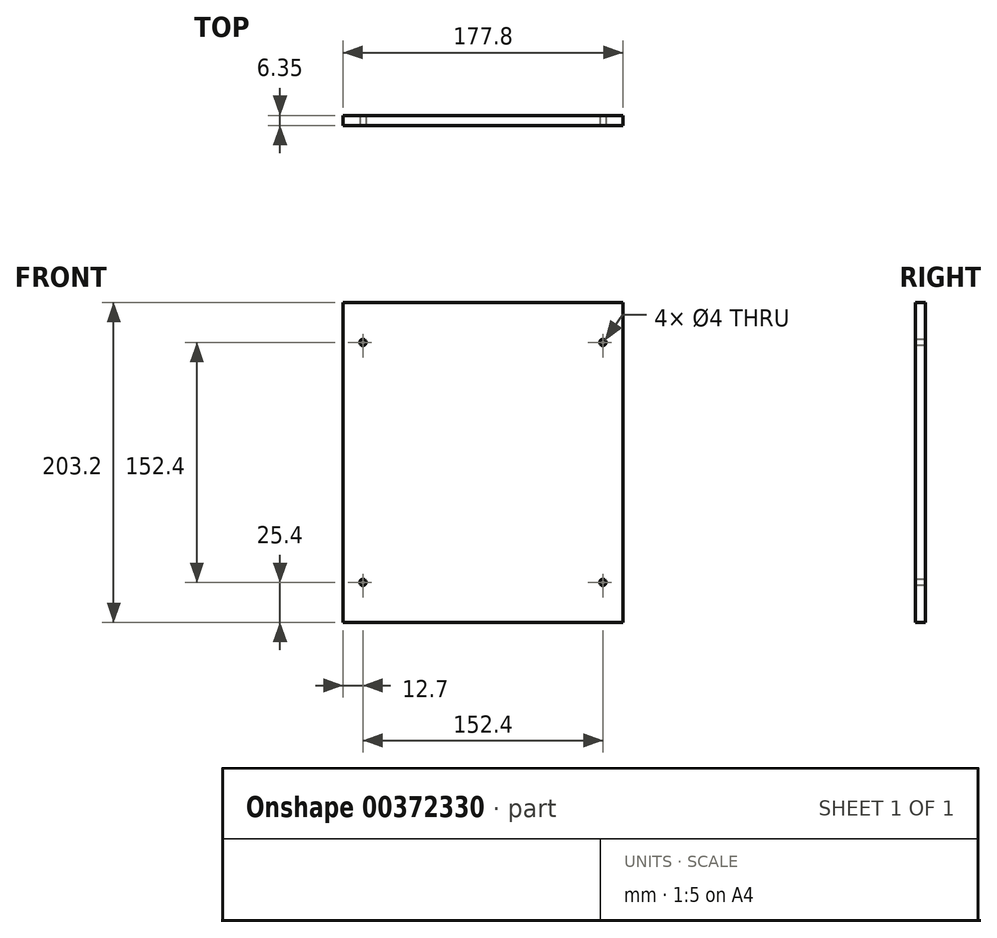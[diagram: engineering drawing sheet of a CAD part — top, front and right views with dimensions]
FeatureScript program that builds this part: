
annotation { "Feature Type Name" : "Feature", "Feature Type Description" : "" }
export const myFeature = defineFeature(function(context is Context, id is Id, definition is map)
    precondition{}
    {
        {
            var Q0;
            Q0=qCreatedBy(makeId("Front.planeOp"),FACE);
            var sketch = newSketch(context, id + "F0", { "sketchPlane" : qUnion([Q0])});
            skLineSegment(sketch, "E0.bottom", {"start": v(88.9, 101.6) * mm, "end": v(-88.9, 101.6) * mm});
            skLineSegment(sketch, "E0.top", {"start": v(88.9, -101.6) * mm, "end": v(-88.9, -101.6) * mm});
            skLineSegment(sketch, "E0.left", {"start": v(88.9, 101.6) * mm, "end": v(88.9, -101.6) * mm});
            skLineSegment(sketch, "E0.right", {"start": v(-88.9, 101.6) * mm, "end": v(-88.9, -101.6) * mm});
            skPoint(sketch, "E0.middle", {"position": v(0, 0) * mm});
            skLineSegment(sketch, "E1", {"start": v(-88.9, 101.6) * mm, "end": v(88.9, -101.6) * mm, "construction": true});
            skLineSegment(sketch, "E2", {"start": v(-88.9, -101.6) * mm, "end": v(88.9, 101.6) * mm, "construction": true});
            skSolve(sketch);
        }
        {
            var Q0;
            Q0 = qSketchRegion(id + "F0", true);
            extrude(context, id + "F1", {"entities" : qUnion([Q0]), "depth" : 6.35 * mm});
        }
        {
            var Q0;
            Q0=makeQuery(id+"F1.opExtrude","CAP_FACE",FACE,{"disambiguationData":[OSD([sQuery(id+"F0.wireOp",EDGE,"E0.bottom"),sQuery(id+"F0.wireOp",EDGE,"E0.top"),sQuery(id+"F0.wireOp",EDGE,"E0.left"),sQuery(id+"F0.wireOp",EDGE,"E0.right")])],"isStart":false});
            var sketch = newSketch(context, id + "F2", { "sketchPlane" : qUnion([Q0])});
            skLineSegment(sketch, "E3.bottom", {"start": v(76.2, 76.2) * mm, "end": v(-76.2, 76.2) * mm, "construction": true});
            skLineSegment(sketch, "E3.top", {"start": v(76.2, -76.2) * mm, "end": v(-76.2, -76.2) * mm, "construction": true});
            skLineSegment(sketch, "E3.left", {"start": v(76.2, 76.2) * mm, "end": v(76.2, -76.2) * mm, "construction": true});
            skLineSegment(sketch, "E3.right", {"start": v(-76.2, 76.2) * mm, "end": v(-76.2, -76.2) * mm, "construction": true});
            skPoint(sketch, "E3.middle", {"position": v(0, 0) * mm});
            skLineSegment(sketch, "E4", {"start": v(-76.2, 76.2) * mm, "end": v(76.2, -76.2) * mm, "construction": true});
            skLineSegment(sketch, "E5", {"start": v(76.2, 76.2) * mm, "end": v(-76.2, -76.2) * mm, "construction": true});
            skSolve(sketch);
        }
        {
            var Q0;
            Q0=sQuery(id+"F2.wireOp",VERTEX,"E3.right.start");
            var Q1;
            Q1=sQuery(id+"F2.wireOp",VERTEX,"E3.left.start");
            var Q2;
            Q2=sQuery(id+"F2.wireOp",VERTEX,"E3.top.end");
            var Q3;
            Q3=sQuery(id+"F2.wireOp",VERTEX,"E3.left.end");
            var Q4;
            Q4=makeQuery(id+"F1.opExtrude","SWEPT_BODY",BODY,{"disambiguationData":[OSD([sQuery(id+"F0.wireOp",EDGE,"E0.bottom"),sQuery(id+"F0.wireOp",EDGE,"E0.top"),sQuery(id+"F0.wireOp",EDGE,"E0.left"),sQuery(id+"F0.wireOp",EDGE,"E0.right")])]});
            hole(context, id + "F3", {"style" : HoleStyle.SIMPLE, "endStyle" : HoleEndStyle.THROUGH, "holeDiameter" : 4 * mm, "isTappedThrough" : true, "tappedDepth" : 12.7 * mm, "tapClearance" : 3, "locations" : qUnion([Q0, Q1, Q2, Q3]), "scope" : qUnion([Q4])});
        }
    });
